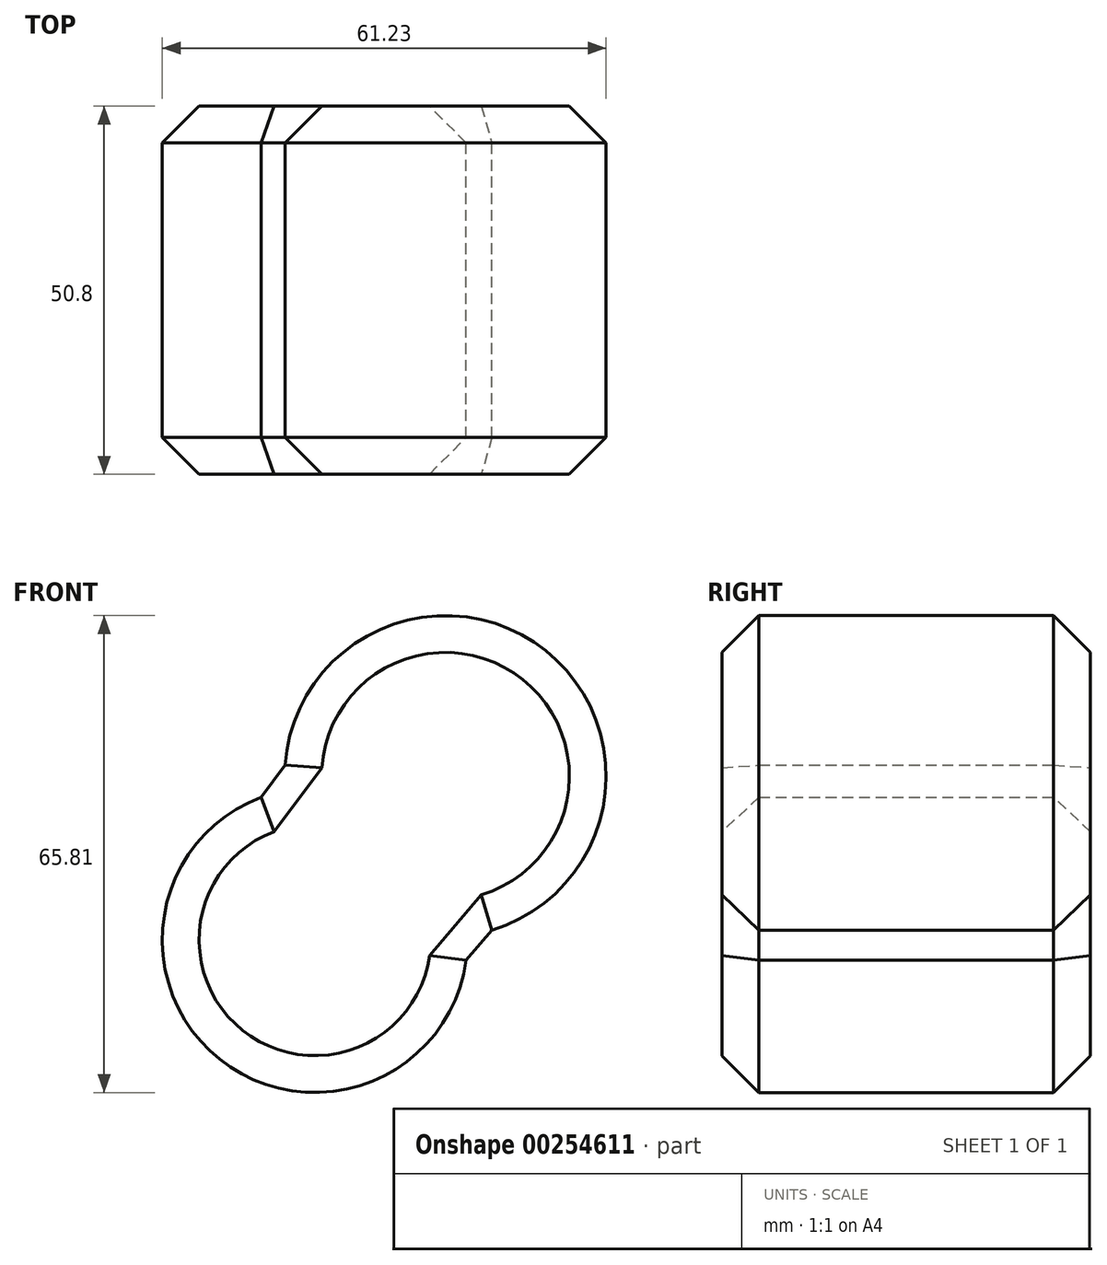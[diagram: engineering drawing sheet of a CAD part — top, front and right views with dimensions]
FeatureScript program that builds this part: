
annotation { "Feature Type Name" : "Feature", "Feature Type Description" : "" }
export const myFeature = defineFeature(function(context is Context, id is Id, definition is map)
    precondition{}
    {
        {
            var Q0;
            Q0=qCreatedBy(makeId("Front.planeOp"),FACE);
            var sketch = newSketch(context, id + "F0", { "sketchPlane" : qUnion([Q0])});
            skCircle(sketch, "E0", {"center": v(0, 0) * mm, "radius": 21.05 * mm});
            skCircle(sketch, "E1", {"center": v(18.01, 22.59) * mm, "radius": 22.17 * mm});
            skSolve(sketch);
        }
        {
            var Q0;
            {var subQ0=sQuery(id+"F0.wireOp",EDGE,"E1");var subQ1=sQuery(id+"F0.wireOp",EDGE,"E0");var subQ2=makeQuery(id+"F0.imprint","INTERSECT",VERTEX,{"disambiguationData":[OD(0.0)],"derivedFrom":[subQ1,subQ0]});Q0=makeQuery(id+"F0.imprint","IMPRINT",FACE,{"disambiguationData":[TD([[makeQuery(id+"F0.imprint","IMPRINT",EDGE,{"disambiguationData":[TD([[subQ2,-1.0]])],"derivedFrom":subQ1}),1.0]])]});}
            var Q1;
            {var subQ0=sQuery(id+"F0.wireOp",EDGE,"E1");var subQ1=sQuery(id+"F0.wireOp",EDGE,"E0");var subQ2=makeQuery(id+"F0.imprint","INTERSECT",VERTEX,{"disambiguationData":[OD(0.0)],"derivedFrom":[subQ1,subQ0]});Q1=makeQuery(id+"F0.imprint","IMPRINT",FACE,{"disambiguationData":[TD([[makeQuery(id+"F0.imprint","IMPRINT",EDGE,{"disambiguationData":[TD([[subQ2,1.0]])],"derivedFrom":subQ1}),1.0]])]});}
            extrude(context, id + "F1", {"entities" : qUnion([Q0, Q1]), "depth" : 25.4 * mm});
        }
        {
            var Q0;
            Q0 = qSketchRegion(id + "F0", true);
            extrude(context, id + "F2", {"entities" : qUnion([Q0]), "operationType" : NewBodyOperationType.ADD, "depth" : 50.8 * mm});
        }
        {
            var Q0;
            Q0=makeQuery(id+"F2.opExtrude","CAP_EDGE",EDGE,{"disambiguationData":[OSD([sQuery(id+"F0.wireOp",EDGE,"E0")])],"isStart":false});
            var Q1;
            Q1=makeQuery(id+"F2.opExtrude","CAP_EDGE",EDGE,{"disambiguationData":[OSD([sQuery(id+"F0.wireOp",EDGE,"E1")])],"isStart":false});
            var Q2;
            Q2=makeQuery(id+"F1.opExtrude","CAP_EDGE",EDGE,{"disambiguationData":[OSD([sQuery(id+"F0.wireOp",EDGE,"E0")])],"isStart":true});
            var Q3;
            Q3=makeQuery(id+"F2.opExtrude","CAP_EDGE",EDGE,{"disambiguationData":[OSD([sQuery(id+"F0.wireOp",EDGE,"E1")])],"isStart":true});
            var Q4;
            Q4=makeQuery(id+"F2.opExtrude","SWEPT_FACE",FACE,{"disambiguationData":[OSD([sQuery(id+"F0.wireOp",EDGE,"E1")])]});
            var Q5;
            {var subQ0=sQuery(id+"F0.wireOp",EDGE,"E0");Q5=makeQuery(id+"F2.boolean.opBoolean","MERGE",FACE,{"derivedFrom":[makeQuery(id+"F1.opExtrude","SWEPT_FACE",FACE,{"disambiguationData":[OSD([subQ0])]}),makeQuery(id+"F2.opExtrude","SWEPT_FACE",FACE,{"disambiguationData":[OSD([subQ0])]})]});}
            chamfer(context, id + "F3", {"entities" : qUnion([Q0, Q1, Q2, Q3, Q4, Q5]), "width" : 5.08 * mm, "tangentPropagation" : true});
        }
    });
